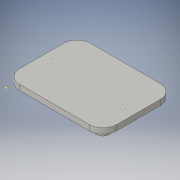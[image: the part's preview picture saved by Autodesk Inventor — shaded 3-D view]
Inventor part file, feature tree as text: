
AUTODESK INVENTOR PART (.ipt)
format: ipt  version: 2016 (Build 200138000, 138)  size: 180,224 bytes
history: native  units: in
note: dims shown in document units (in); Inventor stores cm internally (conversion verified against a paired STEP export)
features: sketch x6, extrude x5, fillet x1, projected_geometry x1
ambient origin geometry x8: Origin, YZ Plane, XZ Plane, XY Plane, X Axis, Y Axis, Z Axis, Center Point
bodies: Solid1 (feature_tree)
feature tree (13):
  extrude  "Extrusion1"  Depth=2.6in
  extrude  "Extrusion2"  Depth=0.2in
  extrude  "Extrusion3"  Depth=0.12in
  sketch  "Sketch4"  dims[d7=0.12in d8=0.12in d9=0.102in d10=0.0in]
  extrude  "Extrusion4"  Depth=0.102in
  fillet  "Fillet1"  Radius=0.102in
  extrude  "Extrusion5"  Depth=0.4in
  sketch  "Sketch1"  dims[d0=3.55in d1=2.6in]
  sketch  "Sketch2"  dims[d2=0.2in d3=0.0in d4=0.4625in]
  projected_geometry  "Projected Loop1"
  sketch  "Sketch3"  dims[d5=0.12in d6=0.12in]
  sketch  "Sketch5"  dims[d11=0.253in d12=0.4in]
  sketch  "Sketch6"  dims[d14=0.253in d15=0.63in d16=0.16in d17=0.0in d18=0.23in d19=0.325in d20=0.35in d21=0.0in d22=0.5in d23=0.18in d24=0.18in d25=0.3725in d26=0.0in]
